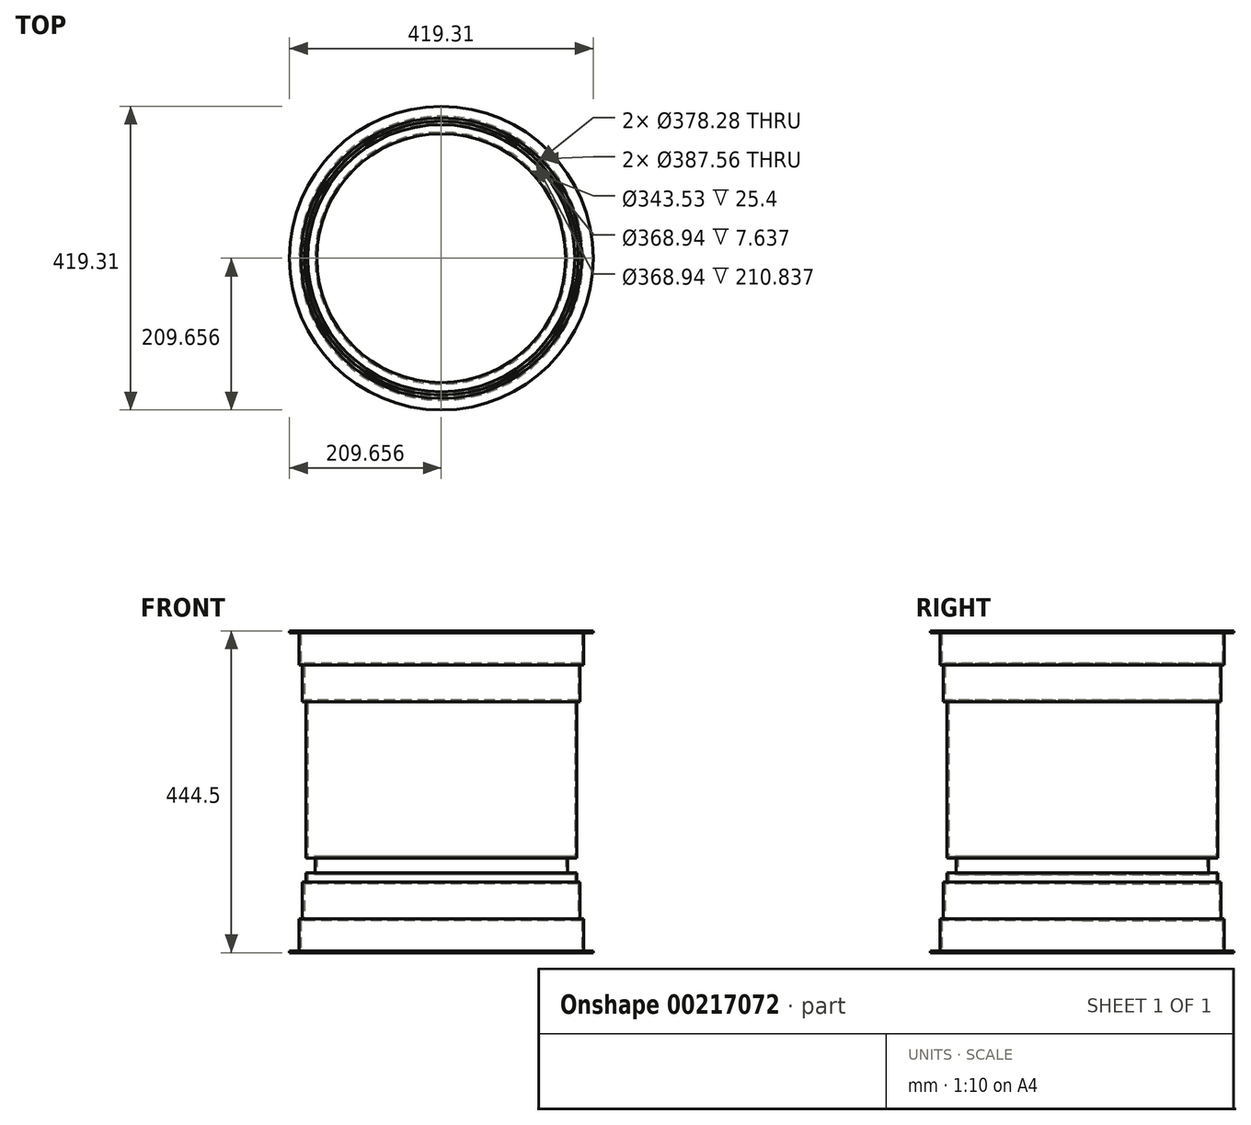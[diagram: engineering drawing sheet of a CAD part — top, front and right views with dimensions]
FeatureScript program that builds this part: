
annotation { "Feature Type Name" : "Feature", "Feature Type Description" : "" }
export const myFeature = defineFeature(function(context is Context, id is Id, definition is map)
    precondition{}
    {
        {
            var Q0;
            Q0=qCreatedBy(makeId("Top.planeOp"),FACE);
            var sketch = newSketch(context, id + "F0", { "sketchPlane" : qUnion([Q0])});
            skCircle(sketch, "E0", {"center": v(-48.75, -41.92) * mm, "radius": 184.47 * mm});
            skCircle(sketch, "E1.0", {"center": v(-48.75, -41.92) * mm, "radius": 171.77 * mm});
            skCircle(sketch, "E2", {"center": v(-48.75, -41.92) * mm, "radius": 189.14 * mm});
            skCircle(sketch, "E3", {"center": v(-48.75, -41.92) * mm, "radius": 193.78 * mm});
            skCircle(sketch, "E4.0", {"center": v(-48.75, -41.92) * mm, "radius": 206.48 * mm});
            skCircle(sketch, "E5.0", {"center": v(-48.75, -41.92) * mm, "radius": 209.65 * mm});
            skSolve(sketch);
        }
        {
            var Q0;
            Q0=makeQuery(id+"F0.imprint","IMPRINT",FACE,{"disambiguationData":[TD([[makeQuery(id+"F0.imprint","IMPRINT",EDGE,{"derivedFrom":sQuery(id+"F0.wireOp",EDGE,"E1.0")}),1.0]])]});
            extrude(context, id + "F1", {"entities" : qUnion([Q0]), "depth" : 6.35 * mm, "symmetric" : true});
        }
        {
            var Q0;
            Q0=makeQuery(id+"F0.imprint","IMPRINT",FACE,{"disambiguationData":[TD([[makeQuery(id+"F0.imprint","IMPRINT",EDGE,{"derivedFrom":sQuery(id+"F0.wireOp",EDGE,"E0")}),1.0]])]});
            extrude(context, id + "F2", {"entities" : qUnion([Q0]), "operationType" : NewBodyOperationType.ADD, "depth" : 25.4 * mm, "symmetric" : true});
        }
        {
            var Q0;
            Q0=makeQuery(id+"F0.imprint","IMPRINT",FACE,{"disambiguationData":[TD([[makeQuery(id+"F0.imprint","IMPRINT",EDGE,{"derivedFrom":sQuery(id+"F0.wireOp",EDGE,"E4.0")}),-1.0]])]});
            extrude(context, id + "F3", {"entities" : qUnion([Q0]), "depth" : 279.4 * mm, "symmetric" : true});
        }
        {
            var Q0;
            Q0=makeQuery(id+"F0.imprint","IMPRINT",FACE,{"disambiguationData":[TD([[makeQuery(id+"F0.imprint","IMPRINT",EDGE,{"derivedFrom":sQuery(id+"F0.wireOp",EDGE,"E3")}),-1.0]])]});
            extrude(context, id + "F4", {"entities" : qUnion([Q0]), "operationType" : NewBodyOperationType.ADD, "depth" : 444.5 * mm, "symmetric" : true});
        }
        {
            var Q0;
            Q0=makeQuery(id+"F0.imprint","IMPRINT",FACE,{"disambiguationData":[TD([[makeQuery(id+"F0.imprint","IMPRINT",EDGE,{"derivedFrom":sQuery(id+"F0.wireOp",EDGE,"E2")}),-1.0]])]});
            extrude(context, id + "F5", {"entities" : qUnion([Q0]), "operationType" : NewBodyOperationType.ADD, "depth" : 355.6 * mm, "symmetric" : true});
        }
        {
            var Q0;
            Q0=makeQuery(id+"F0.imprint","IMPRINT",FACE,{"disambiguationData":[TD([[makeQuery(id+"F0.imprint","IMPRINT",EDGE,{"derivedFrom":sQuery(id+"F0.wireOp",EDGE,"E0")}),-1.0]])]});
            extrude(context, id + "F6", {"entities" : qUnion([Q0]), "operationType" : NewBodyOperationType.ADD, "depth" : 254 * mm, "symmetric" : true});
        }
        {
            var Q0;
            Q0=makeQuery(id+"F1.opExtrude","CAP_FACE",FACE,{"disambiguationData":[OSD([sQuery(id+"F0.wireOp",EDGE,"E1.0")])],"isStart":false});
            extrude(context, id + "F7", {"entities" : qUnion([Q0]), "operationType" : NewBodyOperationType.REMOVE, "endBound" : BoundingType.THROUGH_ALL, "oppositeDirection" : true, "depth" : 25.4 * mm});
        }
        {
            var Q0;
            Q0=makeQuery(id+"F2.opExtrude","CAP_FACE",FACE,{"disambiguationData":[OSD([sQuery(id+"F0.wireOp",EDGE,"E0"),sQuery(id+"F0.wireOp",EDGE,"E1.0")])],"isStart":true});
            extrude(context, id + "F8", {"entities" : qUnion([Q0]), "operationType" : NewBodyOperationType.ADD, "depth" : 101.6 * mm});
        }
        {
            var Q0;
            Q0=makeQuery(id+"F2.opExtrude","CAP_FACE",FACE,{"disambiguationData":[OSD([sQuery(id+"F0.wireOp",EDGE,"E0"),sQuery(id+"F0.wireOp",EDGE,"E1.0")])],"isStart":false});
            extrude(context, id + "F9", {"entities" : qUnion([Q0]), "operationType" : NewBodyOperationType.REMOVE, "oppositeDirection" : true, "depth" : 101.6 * mm});
        }
        {
            var Q0;
            Q0=makeQuery(id+"F3.opExtrude","CAP_FACE",FACE,{"disambiguationData":[OSD([sQuery(id+"F0.wireOp",EDGE,"E4.0"),sQuery(id+"F0.wireOp",EDGE,"E5.0")])],"isStart":false});
            var Q1;
            Q1=makeQuery(id+"F4.opExtrude","CAP_FACE",FACE,{"disambiguationData":[OSD([sQuery(id+"F0.wireOp",EDGE,"E3"),sQuery(id+"F0.wireOp",EDGE,"E4.0")])],"isStart":false});
            extrude(context, id + "F10", {"entities" : qUnion([Q0]), "operationType" : NewBodyOperationType.ADD, "endBound" : BoundingType.UP_TO_SURFACE, "endBoundEntityFace" : qUnion([Q1]), "depth" : 25.4 * mm});
        }
        {
            var Q0;
            Q0=makeQuery(id+"F3.opExtrude","CAP_FACE",FACE,{"disambiguationData":[OSD([sQuery(id+"F0.wireOp",EDGE,"E4.0"),sQuery(id+"F0.wireOp",EDGE,"E5.0")])],"isStart":true});
            var Q1;
            Q1=makeQuery(id+"F4.opExtrude","CAP_FACE",FACE,{"disambiguationData":[OSD([sQuery(id+"F0.wireOp",EDGE,"E3"),sQuery(id+"F0.wireOp",EDGE,"E4.0")])],"isStart":true});
            extrude(context, id + "F11", {"entities" : qUnion([Q0]), "operationType" : NewBodyOperationType.ADD, "endBound" : BoundingType.UP_TO_SURFACE, "endBoundEntityFace" : qUnion([Q1]), "depth" : 25.4 * mm});
        }
        {
            var Q0;
            {var subQ0=sQuery(id+"F0.wireOp",EDGE,"E5.0");Q0=makeQuery(id+"F11.boolean.opBoolean","MERGE",FACE,{"derivedFrom":[makeQuery(id+"F10.boolean.opBoolean","MERGE",FACE,{"derivedFrom":[makeQuery(id+"F3.opExtrude","SWEPT_FACE",FACE,{"disambiguationData":[OSD([subQ0])]}),makeQuery(id+"F10.opExtrude","SWEPT_FACE",FACE,{"disambiguationData":[OSD([subQ0])]})]}),makeQuery(id+"F11.opExtrude","SWEPT_FACE",FACE,{"disambiguationData":[OSD([subQ0])]})]});}
            shell(context, id + "F12", {"entities" : qUnion([Q0]), "thickness" : 2.54 * mm});
        }
        {
            var Q0;
            Q0=makeQuery(id+"F4.opExtrude","CAP_EDGE",EDGE,{"disambiguationData":[OSD([sQuery(id+"F0.wireOp",EDGE,"E3")])],"isStart":true});
            var Q1;
            Q1=makeQuery(id+"F5.opExtrude","CAP_EDGE",EDGE,{"disambiguationData":[OSD([sQuery(id+"F0.wireOp",EDGE,"E2")])],"isStart":true});
            var Q2;
            Q2=makeQuery(id+"F6.opExtrude","CAP_EDGE",EDGE,{"disambiguationData":[OSD([sQuery(id+"F0.wireOp",EDGE,"E0")])],"isStart":true});
            var Q3;
            Q3=makeQuery(id+"F6.opExtrude","CAP_EDGE",EDGE,{"disambiguationData":[OSD([sQuery(id+"F0.wireOp",EDGE,"E0")])],"isStart":false});
            var Q4;
            Q4=makeQuery(id+"F5.opExtrude","CAP_EDGE",EDGE,{"disambiguationData":[OSD([sQuery(id+"F0.wireOp",EDGE,"E2")])],"isStart":false});
            var Q5;
            Q5=makeQuery(id+"F4.opExtrude","CAP_EDGE",EDGE,{"disambiguationData":[OSD([sQuery(id+"F0.wireOp",EDGE,"E3")])],"isStart":false});
            fillet(context, id + "F13", {"entities" : qUnion([Q0, Q1, Q2, Q3, Q4, Q5]), "radius" : 5.08 * mm, "tangentPropagation" : true, "allowEdgeOverflow" : false});
        }
    });
